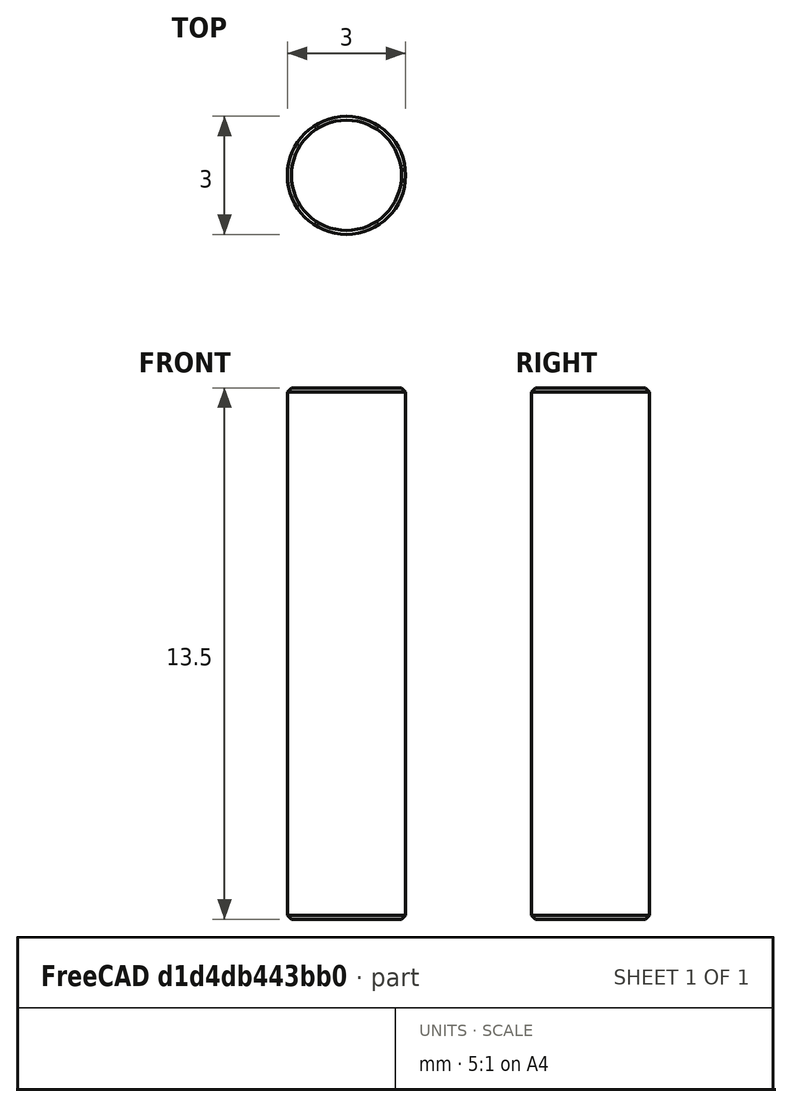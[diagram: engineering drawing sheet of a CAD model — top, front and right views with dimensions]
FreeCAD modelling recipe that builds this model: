
FCSTD DOCUMENT  (FreeCAD 0.20R29603 (Git))
Label: magnet_13.5x3mm
License: All rights reserved
LicenseURL: http://en.wikipedia.org/wiki/All_rights_reserved
objects: Sketcher::SketchObject×1, PartDesign::Pad×1, PartDesign::Chamfer×1, PartDesign::Body×1
note: 6 computed .brp shape members not serialized (recipe doc carries the construction recipe); baked Part::Feature solids carry a one-line shape summary decoded from their .brp

FEATURE [Sketcher::SketchObject] Sketch
  FullyConstrained = false
  MapMode = 5
  Support = -> [XY_Plane]
  sketch-geometry (1):
    g0: Circle CenterX=0 CenterY=0 CenterZ=0 NormalX=0 NormalY=0 NormalZ=1 AngleXU=0 Radius=1.5
  constraints (2):
    c: Coincident(g0,g-1)
    c: Radius(g0) = 1.5
FEATURE [PartDesign::Pad] Pad
  AllowMultiFace = false
  Direction = (0,0,1)
  Length = 13.5
  Length2 = 100
  Profile = -> Sketch
  Refine = true
  Reversed = true
  Type = 0
FEATURE [PartDesign::Chamfer] Chamfer
  Angle = 45
  Base = -> Pad [Edge2,Edge3]
  BaseFeature = -> Pad
  ChamferType = 0
  FlipDirection = false
  Size = 0.1
  Size2 = 1
  SupportTransform = false
  UseAllEdges = false
FEATURE [PartDesign::Body] Body
  Group = -> [Sketch,Pad,Chamfer]
  Origin = -> Origin
  Tip = -> Chamfer
